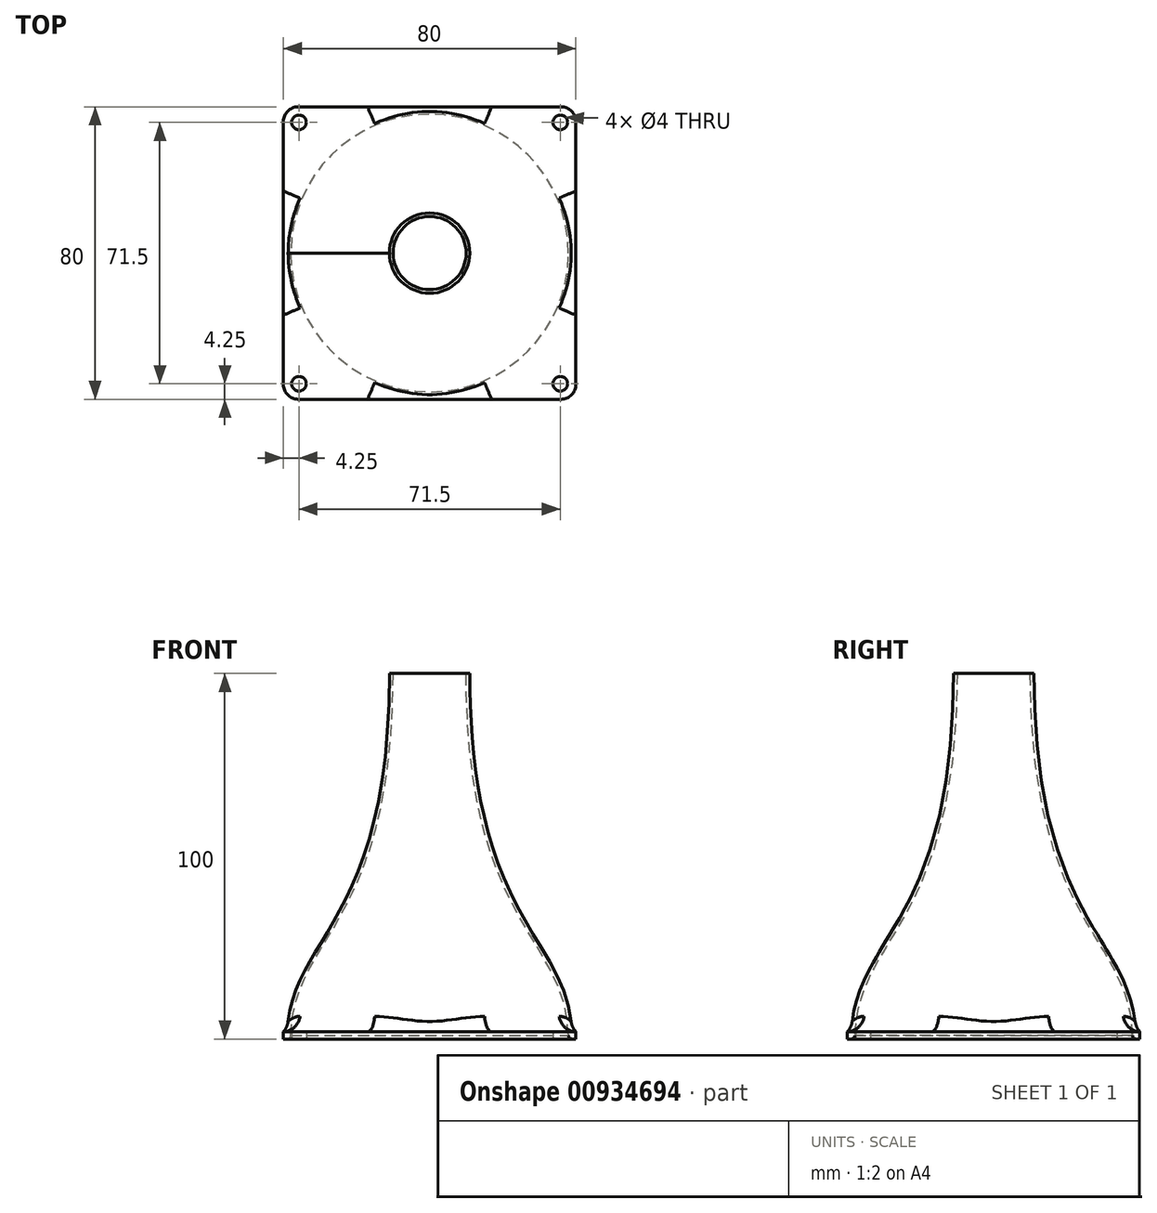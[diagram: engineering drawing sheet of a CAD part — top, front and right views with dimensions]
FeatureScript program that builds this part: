
annotation { "Feature Type Name" : "Feature", "Feature Type Description" : "" }
export const myFeature = defineFeature(function(context is Context, id is Id, definition is map)
    precondition{}
    {
        {
            var Q0;
            Q0=qCreatedBy(makeId("Top.planeOp"),FACE);
            var sketch = newSketch(context, id + "F0", { "sketchPlane" : qUnion([Q0])});
            skLineSegment(sketch, "E0.bottom", {"start": v(-40, 40) * mm, "end": v(40, 40) * mm});
            skLineSegment(sketch, "E0.top", {"start": v(-40, -40) * mm, "end": v(40, -40) * mm});
            skLineSegment(sketch, "E0.left", {"start": v(-40, 40) * mm, "end": v(-40, -40) * mm});
            skLineSegment(sketch, "E0.right", {"start": v(40, 40) * mm, "end": v(40, -40) * mm});
            skCircle(sketch, "E1", {"center": v(-35.75, 35.75) * mm, "radius": 2 * mm});
            skCircle(sketch, "E2", {"center": v(35.75, 35.75) * mm, "radius": 2 * mm});
            skCircle(sketch, "E3", {"center": v(35.75, -35.75) * mm, "radius": 2 * mm});
            skCircle(sketch, "E4", {"center": v(-35.75, -35.75) * mm, "radius": 2 * mm});
            skCircle(sketch, "E5", {"center": v(0, 0) * mm, "radius": 38 * mm});
            skSolve(sketch);
        }
        {
            var Q0;
            Q0=makeQuery(id+"F0.imprint","IMPRINT",FACE,{"disambiguationData":[TD([[makeQuery(id+"F0.imprint","IMPRINT",EDGE,{"derivedFrom":sQuery(id+"F0.wireOp",EDGE,"E0.bottom")}),-1.0]])]});
            extrude(context, id + "F1", {"entities" : qUnion([Q0]), "depth" : 2 * mm, "offsetDistance" : 25 * mm});
        }
        {
            var Q0;
            Q0=qCreatedBy(makeId("Front.planeOp"),FACE);
            var sketch = newSketch(context, id + "F2", { "sketchPlane" : qUnion([Q0])});
            skLineSegment(sketch, "E6", {"start": v(0, 0) * mm, "end": v(-38, 0) * mm, "construction": true});
            skLineSegment(sketch, "E7", {"start": v(0, 0) * mm, "end": v(0, 100) * mm, "construction": true});
            skLineSegment(sketch, "E8", {"start": v(0, 100) * mm, "end": v(-10, 100) * mm, "construction": true});
            skLineSegment(sketch, "E9", {"start": v(-38, 0) * mm, "end": v(-39, 0) * mm});
            skLineSegment(sketch, "E10", {"start": v(-11, 100) * mm, "end": v(-10, 100) * mm});
            skFitSpline(sketch, "E11", {"points": [v(-11, 100) * mm, v(-39, 0) * mm], "startDerivative": vector(0, -209.63) * mm, "endDerivative": vector(0, -85.07) * mm});
            skFitSpline(sketch, "E12", {"points": [v(-38, 0) * mm, v(-10, 100) * mm], "startDerivative": vector(0, 85.07) * mm, "endDerivative": vector(0, 209.63) * mm});
            skSolve(sketch);
        }
        {
            var Q0;
            Q0 = qSketchRegion(id + "F2", true);
            var Q1;
            Q1=sQuery(id+"F2.wireOp",EDGE,"E7");
            revolve(context, id + "F3", {"operationType" : NewBodyOperationType.ADD, "surfaceOperationType" : NewSurfaceOperationType.NEW, "entities" : qUnion([Q0]), "axis" : qUnion([Q1]), "revolveType" : RevolveType.FULL});
        }
        {
            var Q0;
            Q0=makeQuery(id+"F3.boolean.opBoolean","MERGE",EDGE,{"derivedFrom":[makeQuery(id+"F1.opExtrude","CAP_EDGE",EDGE,{"disambiguationData":[OSD([sQuery(id+"F0.wireOp",EDGE,"E5")])],"isStart":true}),makeQuery(id+"F3.opRevolve","SWEPT_EDGE",EDGE,{"disambiguationData":[OSD([sQuery(id+"F2.wireOp",EDGE,"E9"),sQuery(id+"F2.wireOp",EDGE,"E12")])]})]});
            fillet(context, id + "F4", {"entities" : qUnion([Q0]), "radius" : 1 * mm, "tangentPropagation" : true, "allowEdgeOverflow" : false});
        }
        {
            var Q0;
            Q0=makeQuery(id+"F3.boolean.opBoolean","INTERSECT",EDGE,{"derivedFrom":[makeQuery(id+"F1.opExtrude","CAP_FACE",FACE,{"disambiguationData":[OSD([sQuery(id+"F0.wireOp",EDGE,"E0.bottom"),sQuery(id+"F0.wireOp",EDGE,"E0.top"),sQuery(id+"F0.wireOp",EDGE,"E0.left"),sQuery(id+"F0.wireOp",EDGE,"E0.right"),sQuery(id+"F0.wireOp",EDGE,"E1"),sQuery(id+"F0.wireOp",EDGE,"E2"),sQuery(id+"F0.wireOp",EDGE,"E3"),sQuery(id+"F0.wireOp",EDGE,"E4"),sQuery(id+"F0.wireOp",EDGE,"E5")])],"isStart":false}),makeQuery(id+"F3.opRevolve","SWEPT_FACE",FACE,{"disambiguationData":[OSD([sQuery(id+"F2.wireOp",EDGE,"E11")])]})]});
            fillet(context, id + "F5", {"entities" : qUnion([Q0]), "radius" : 5 * mm, "tangentPropagation" : true, "allowEdgeOverflow" : false});
        }
        {
            var Q0;
            Q0=makeQuery(id+"F1.opExtrude","SWEPT_EDGE",EDGE,{"disambiguationData":[OSD([sQuery(id+"F0.wireOp",EDGE,"E0.top"),sQuery(id+"F0.wireOp",EDGE,"E0.right")])]});
            var Q1;
            Q1=makeQuery(id+"F1.opExtrude","SWEPT_EDGE",EDGE,{"disambiguationData":[OSD([sQuery(id+"F0.wireOp",EDGE,"E0.top"),sQuery(id+"F0.wireOp",EDGE,"E0.left")])]});
            var Q2;
            Q2=makeQuery(id+"F1.opExtrude","SWEPT_EDGE",EDGE,{"disambiguationData":[OSD([sQuery(id+"F0.wireOp",EDGE,"E0.bottom"),sQuery(id+"F0.wireOp",EDGE,"E0.right")])]});
            var Q3;
            Q3=makeQuery(id+"F1.opExtrude","SWEPT_EDGE",EDGE,{"disambiguationData":[OSD([sQuery(id+"F0.wireOp",EDGE,"E0.bottom"),sQuery(id+"F0.wireOp",EDGE,"E0.left")])]});
            fillet(context, id + "F6", {"entities" : qUnion([Q0, Q1, Q2, Q3]), "radius" : 4 * mm, "tangentPropagation" : true, "allowEdgeOverflow" : false});
        }
    });
